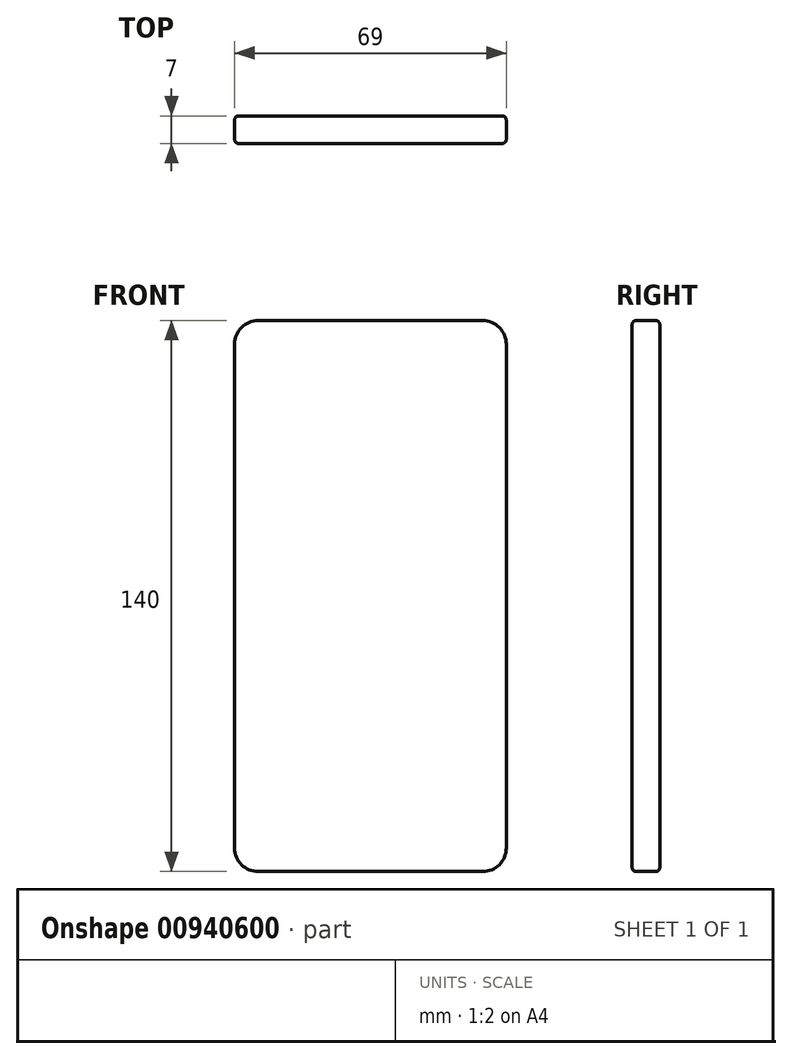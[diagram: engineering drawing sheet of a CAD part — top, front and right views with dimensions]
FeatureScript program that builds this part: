
annotation { "Feature Type Name" : "Feature", "Feature Type Description" : "" }
export const myFeature = defineFeature(function(context is Context, id is Id, definition is map)
    precondition{}
    {
        {
            var Q0;
            Q0=qCreatedBy(makeId("Front.planeOp"),FACE);
            var sketch = newSketch(context, id + "F0", { "sketchPlane" : qUnion([Q0])});
            skLineSegment(sketch, "E0.bottom", {"start": v(-34.5, 70) * mm, "end": v(34.5, 70) * mm});
            skLineSegment(sketch, "E0.top", {"start": v(-34.5, -70) * mm, "end": v(34.5, -70) * mm});
            skLineSegment(sketch, "E0.left", {"start": v(-34.5, 70) * mm, "end": v(-34.5, -70) * mm});
            skLineSegment(sketch, "E0.right", {"start": v(34.5, 70) * mm, "end": v(34.5, -70) * mm});
            skSolve(sketch);
        }
        {
            var Q0;
            Q0 = qSketchRegion(id + "F0", true);
            extrude(context, id + "F1", {"entities" : qUnion([Q0]), "depth" : 7 * mm, "offsetDistance" : 25 * mm});
        }
        {
            var Q0;
            Q0=makeQuery(id+"F1.opExtrude","SWEPT_EDGE",EDGE,{"disambiguationData":[OSD([sQuery(id+"F0.wireOp",EDGE,"E0.bottom"),sQuery(id+"F0.wireOp",EDGE,"E0.right")])]});
            var Q1;
            Q1=makeQuery(id+"F1.opExtrude","SWEPT_EDGE",EDGE,{"disambiguationData":[OSD([sQuery(id+"F0.wireOp",EDGE,"E0.bottom"),sQuery(id+"F0.wireOp",EDGE,"E0.left")])]});
            var Q2;
            Q2=makeQuery(id+"F1.opExtrude","SWEPT_EDGE",EDGE,{"disambiguationData":[OSD([sQuery(id+"F0.wireOp",EDGE,"E0.top"),sQuery(id+"F0.wireOp",EDGE,"E0.right")])]});
            var Q3;
            Q3=makeQuery(id+"F1.opExtrude","SWEPT_EDGE",EDGE,{"disambiguationData":[OSD([sQuery(id+"F0.wireOp",EDGE,"E0.top"),sQuery(id+"F0.wireOp",EDGE,"E0.left")])]});
            fillet(context, id + "F2", {"entities" : qUnion([Q0, Q1, Q2, Q3]), "radius" : 6 * mm, "tangentPropagation" : true, "allowEdgeOverflow" : false});
        }
        {
            var Q0;
            Q0=makeQuery(id+"F1.opExtrude","CAP_EDGE",EDGE,{"disambiguationData":[OSD([sQuery(id+"F0.wireOp",EDGE,"E0.bottom")])],"isStart":false});
            var Q1;
            Q1=makeQuery(id+"F1.opExtrude","CAP_EDGE",EDGE,{"disambiguationData":[OSD([sQuery(id+"F0.wireOp",EDGE,"E0.bottom")])],"isStart":true});
            fillet(context, id + "F3", {"entities" : qUnion([Q0, Q1]), "radius" : 1 * mm, "tangentPropagation" : true, "allowEdgeOverflow" : false});
        }
    });
